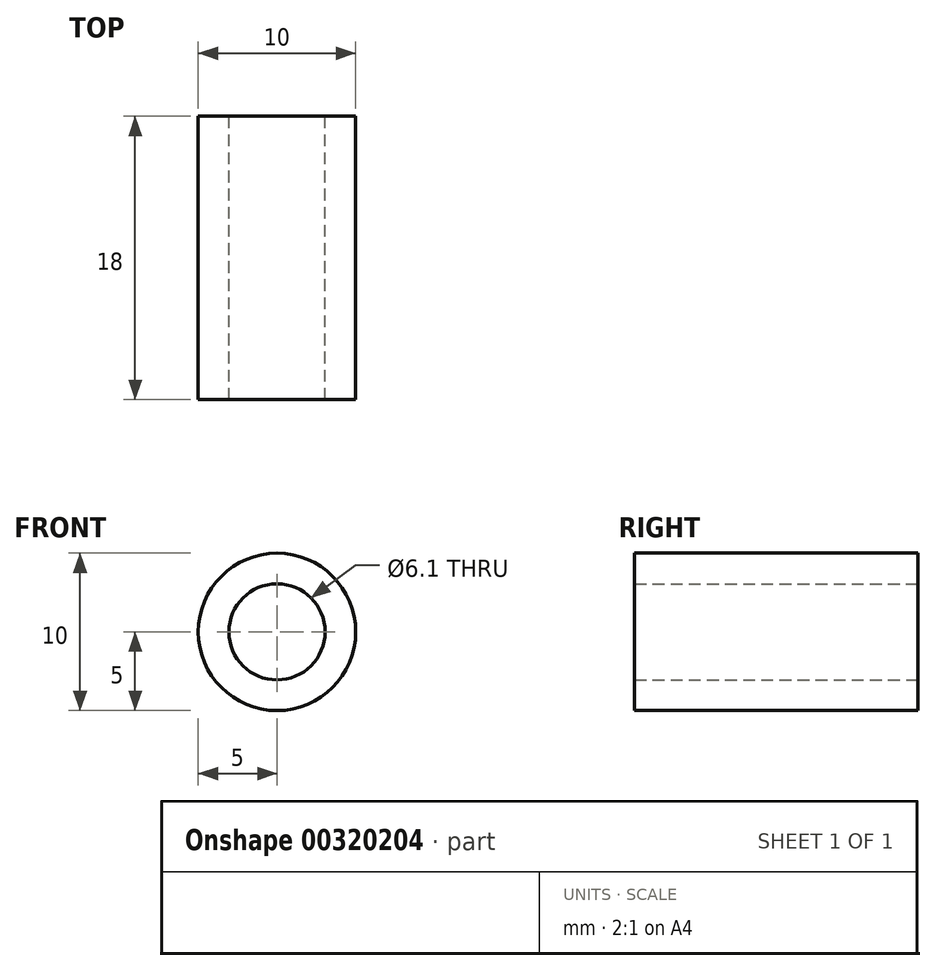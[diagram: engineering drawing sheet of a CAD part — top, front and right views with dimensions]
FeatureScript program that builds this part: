
annotation { "Feature Type Name" : "Feature", "Feature Type Description" : "" }
export const myFeature = defineFeature(function(context is Context, id is Id, definition is map)
    precondition{}
    {
        {
            var Q0;
            Q0=qCreatedBy(makeId("Front.planeOp"),FACE);
            var sketch = newSketch(context, id + "F0", { "sketchPlane" : qUnion([Q0])});
            skCircle(sketch, "E0", {"center": v(0, 0) * mm, "radius": 5 * mm});
            skCircle(sketch, "E1", {"center": v(0, 0) * mm, "radius": 3.05 * mm});
            skSolve(sketch);
        }
        {
            var Q0;
            Q0 = qSketchRegion(id + "F0", true);
            extrude(context, id + "F1", {"entities" : qUnion([Q0]), "endBound" : BoundingType.SYMMETRIC, "depth" : 18 * mm});
        }
    });
